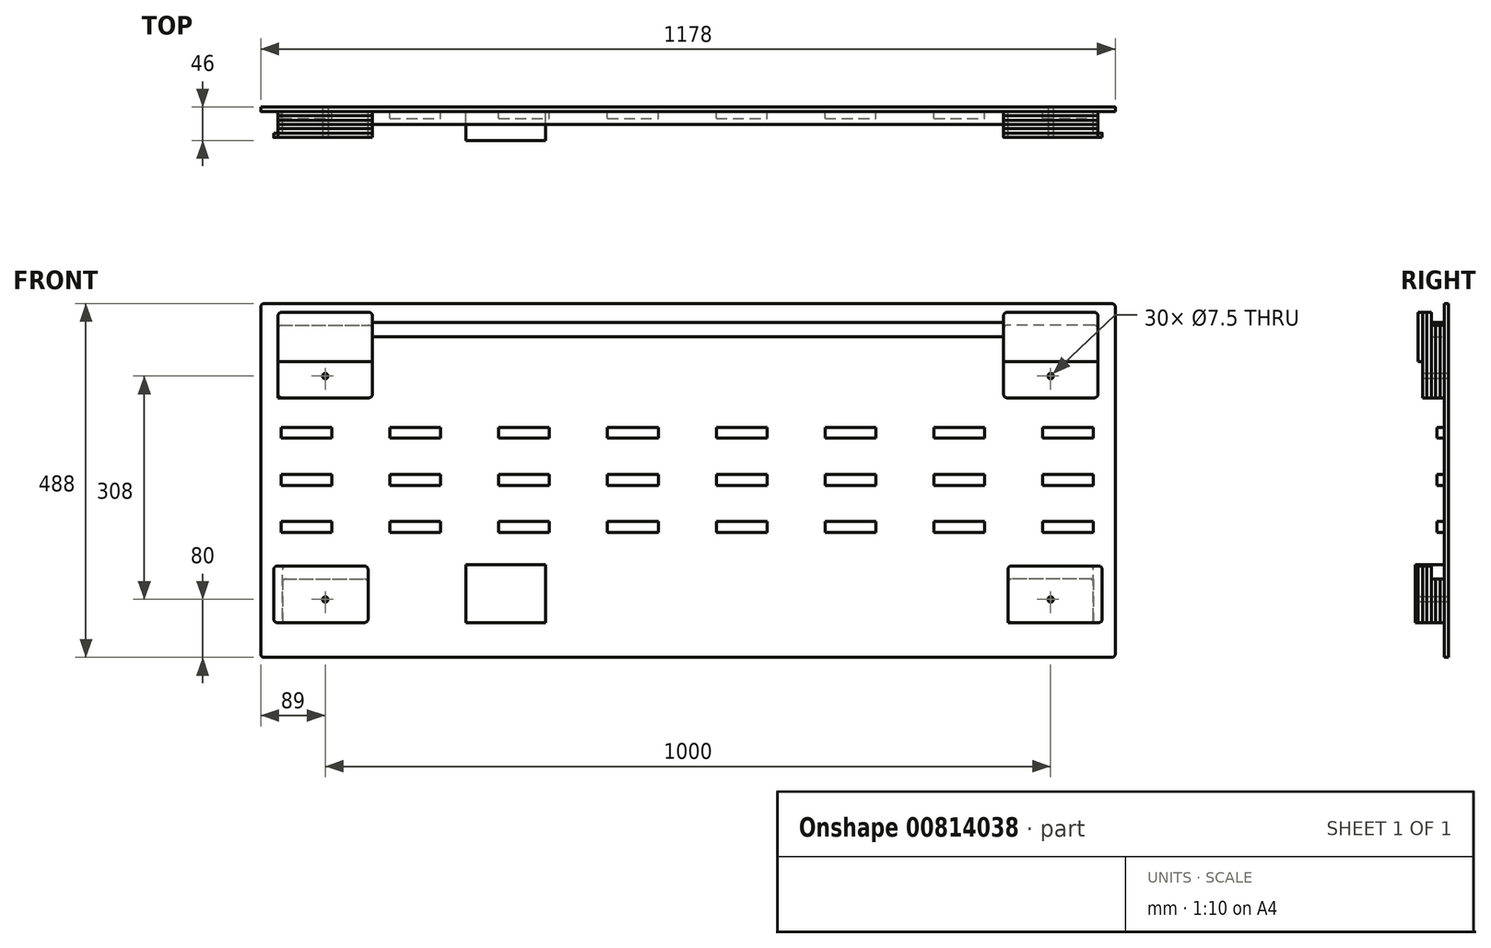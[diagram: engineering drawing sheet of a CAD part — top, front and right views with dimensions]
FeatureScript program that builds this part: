
annotation { "Feature Type Name" : "Feature", "Feature Type Description" : "" }
export const myFeature = defineFeature(function(context is Context, id is Id, definition is map)
    precondition{}
    {
        {
            var Q0;
            Q0=qCreatedBy(makeId("Front.planeOp"),FACE);
            var sketch = newSketch(context, id + "F0", { "sketchPlane" : qUnion([Q0])});
            skLineSegment(sketch, "E0.bottom", {"start": v(-589, 244) * mm, "end": v(589, 244) * mm});
            skLineSegment(sketch, "E0.top", {"start": v(-589, -244) * mm, "end": v(589, -244) * mm});
            skLineSegment(sketch, "E0.left", {"start": v(-589, 244) * mm, "end": v(-589, -244) * mm});
            skLineSegment(sketch, "E0.right", {"start": v(589, 244) * mm, "end": v(589, -244) * mm});
            skPoint(sketch, "E0.middle", {"position": v(0, 0) * mm});
            skSolve(sketch);
        }
        {
            var Q0;
            Q0 = qSketchRegion(id + "F0", true);
            extrude(context, id + "F1", {"entities" : qUnion([Q0]), "depth" : 6 * mm, "offsetDistance" : 25 * mm});
        }
        {
            var Q0;
            Q0=makeQuery(id+"F1.opExtrude","CAP_FACE",FACE,{"disambiguationData":[OSD([sQuery(id+"F0.wireOp",EDGE,"E0.bottom"),sQuery(id+"F0.wireOp",EDGE,"E0.top"),sQuery(id+"F0.wireOp",EDGE,"E0.left"),sQuery(id+"F0.wireOp",EDGE,"E0.right")])],"isStart":false});
            var sketch = newSketch(context, id + "F2", { "sketchPlane" : qUnion([Q0])});
            skLineSegment(sketch, "E1.bottom", {"start": v(-561, 73.35) * mm, "end": v(-491, 73.35) * mm});
            skLineSegment(sketch, "E1.top", {"start": v(-561, 58.35) * mm, "end": v(-491, 58.35) * mm});
            skLineSegment(sketch, "E1.left", {"start": v(-561, 73.35) * mm, "end": v(-561, 58.35) * mm});
            skLineSegment(sketch, "E1.right", {"start": v(-491, 73.35) * mm, "end": v(-491, 58.35) * mm});
            skLineSegment(sketch, "E2", {"start": v(-595.7, 2.32) * mm, "end": v(592.3, 2.32) * mm, "construction": true});
            skLineSegment(sketch, "E3", {"start": v(4.3, 246.32) * mm, "end": v(4.3, -241.68) * mm, "construction": true});
            skLineSegment(sketch, "E4", {"start": v(-595.7, 87.58) * mm, "end": v(592.3, 87.58) * mm, "construction": true});
            skLineSegment(sketch, "E5", {"start": v(-595.7, -82.94) * mm, "end": v(592.3, -82.94) * mm, "construction": true});
            skLineSegment(sketch, "E6", {"start": v(-565.56, 246.32) * mm, "end": v(-565.56, -241.68) * mm, "construction": true});
            skLineSegment(sketch, "E7", {"start": v(574.16, 246.32) * mm, "end": v(574.16, -241.68) * mm, "construction": true});
            skLineSegment(sketch, "E8.0.1.0", {"start": v(-561, 8.35) * mm, "end": v(-491, 8.35) * mm});
            skLineSegment(sketch, "E8.0.1.1", {"start": v(-491, 8.35) * mm, "end": v(-491, -6.65) * mm});
            skLineSegment(sketch, "E8.0.1.2", {"start": v(-561, 8.35) * mm, "end": v(-561, -6.65) * mm});
            skLineSegment(sketch, "E8.0.1.3", {"start": v(-561, -6.65) * mm, "end": v(-491, -6.65) * mm});
            skLineSegment(sketch, "E8.0.2.0", {"start": v(-561, -56.65) * mm, "end": v(-491, -56.65) * mm});
            skLineSegment(sketch, "E8.0.2.1", {"start": v(-491, -56.65) * mm, "end": v(-491, -71.65) * mm});
            skLineSegment(sketch, "E8.0.2.2", {"start": v(-561, -56.65) * mm, "end": v(-561, -71.65) * mm});
            skLineSegment(sketch, "E8.0.2.3", {"start": v(-561, -71.65) * mm, "end": v(-491, -71.65) * mm});
            skLineSegment(sketch, "E8.1.0.0", {"start": v(-411, 73.35) * mm, "end": v(-341, 73.35) * mm});
            skLineSegment(sketch, "E8.1.0.1", {"start": v(-341, 73.35) * mm, "end": v(-341, 58.35) * mm});
            skLineSegment(sketch, "E8.1.0.2", {"start": v(-411, 73.35) * mm, "end": v(-411, 58.35) * mm});
            skLineSegment(sketch, "E8.1.0.3", {"start": v(-411, 58.35) * mm, "end": v(-341, 58.35) * mm});
            skLineSegment(sketch, "E8.1.1.0", {"start": v(-411, 8.35) * mm, "end": v(-341, 8.35) * mm});
            skLineSegment(sketch, "E8.1.1.1", {"start": v(-341, 8.35) * mm, "end": v(-341, -6.65) * mm});
            skLineSegment(sketch, "E8.1.1.2", {"start": v(-411, 8.35) * mm, "end": v(-411, -6.65) * mm});
            skLineSegment(sketch, "E8.1.1.3", {"start": v(-411, -6.65) * mm, "end": v(-341, -6.65) * mm});
            skLineSegment(sketch, "E8.1.2.0", {"start": v(-411, -56.65) * mm, "end": v(-341, -56.65) * mm});
            skLineSegment(sketch, "E8.1.2.1", {"start": v(-341, -56.65) * mm, "end": v(-341, -71.65) * mm});
            skLineSegment(sketch, "E8.1.2.2", {"start": v(-411, -56.65) * mm, "end": v(-411, -71.65) * mm});
            skLineSegment(sketch, "E8.1.2.3", {"start": v(-411, -71.65) * mm, "end": v(-341, -71.65) * mm});
            skLineSegment(sketch, "E8.2.0.0", {"start": v(-261, 73.35) * mm, "end": v(-191, 73.35) * mm});
            skLineSegment(sketch, "E8.2.0.1", {"start": v(-191, 73.35) * mm, "end": v(-191, 58.35) * mm});
            skLineSegment(sketch, "E8.2.0.2", {"start": v(-261, 73.35) * mm, "end": v(-261, 58.35) * mm});
            skLineSegment(sketch, "E8.2.0.3", {"start": v(-261, 58.35) * mm, "end": v(-191, 58.35) * mm});
            skLineSegment(sketch, "E8.2.1.0", {"start": v(-261, 8.35) * mm, "end": v(-191, 8.35) * mm});
            skLineSegment(sketch, "E8.2.1.1", {"start": v(-191, 8.35) * mm, "end": v(-191, -6.65) * mm});
            skLineSegment(sketch, "E8.2.1.2", {"start": v(-261, 8.35) * mm, "end": v(-261, -6.65) * mm});
            skLineSegment(sketch, "E8.2.1.3", {"start": v(-261, -6.65) * mm, "end": v(-191, -6.65) * mm});
            skLineSegment(sketch, "E8.2.2.0", {"start": v(-261, -56.65) * mm, "end": v(-191, -56.65) * mm});
            skLineSegment(sketch, "E8.2.2.1", {"start": v(-191, -56.65) * mm, "end": v(-191, -71.65) * mm});
            skLineSegment(sketch, "E8.2.2.2", {"start": v(-261, -56.65) * mm, "end": v(-261, -71.65) * mm});
            skLineSegment(sketch, "E8.2.2.3", {"start": v(-261, -71.65) * mm, "end": v(-191, -71.65) * mm});
            skLineSegment(sketch, "E8.3.0.0", {"start": v(-111, 73.35) * mm, "end": v(-41, 73.35) * mm});
            skLineSegment(sketch, "E8.3.0.1", {"start": v(-41, 73.35) * mm, "end": v(-41, 58.35) * mm});
            skLineSegment(sketch, "E8.3.0.2", {"start": v(-111, 73.35) * mm, "end": v(-111, 58.35) * mm});
            skLineSegment(sketch, "E8.3.0.3", {"start": v(-111, 58.35) * mm, "end": v(-41, 58.35) * mm});
            skLineSegment(sketch, "E8.3.1.0", {"start": v(-111, 8.35) * mm, "end": v(-41, 8.35) * mm});
            skLineSegment(sketch, "E8.3.1.1", {"start": v(-41, 8.35) * mm, "end": v(-41, -6.65) * mm});
            skLineSegment(sketch, "E8.3.1.2", {"start": v(-111, 8.35) * mm, "end": v(-111, -6.65) * mm});
            skLineSegment(sketch, "E8.3.1.3", {"start": v(-111, -6.65) * mm, "end": v(-41, -6.65) * mm});
            skLineSegment(sketch, "E8.3.2.0", {"start": v(-111, -56.65) * mm, "end": v(-41, -56.65) * mm});
            skLineSegment(sketch, "E8.3.2.1", {"start": v(-41, -56.65) * mm, "end": v(-41, -71.65) * mm});
            skLineSegment(sketch, "E8.3.2.2", {"start": v(-111, -56.65) * mm, "end": v(-111, -71.65) * mm});
            skLineSegment(sketch, "E8.3.2.3", {"start": v(-111, -71.65) * mm, "end": v(-41, -71.65) * mm});
            skLineSegment(sketch, "E8.4.0.0", {"start": v(39, 73.35) * mm, "end": v(109, 73.35) * mm});
            skLineSegment(sketch, "E8.4.0.1", {"start": v(109, 73.35) * mm, "end": v(109, 58.35) * mm});
            skLineSegment(sketch, "E8.4.0.2", {"start": v(39, 73.35) * mm, "end": v(39, 58.35) * mm});
            skLineSegment(sketch, "E8.4.0.3", {"start": v(39, 58.35) * mm, "end": v(109, 58.35) * mm});
            skLineSegment(sketch, "E8.4.1.0", {"start": v(39, 8.35) * mm, "end": v(109, 8.35) * mm});
            skLineSegment(sketch, "E8.4.1.1", {"start": v(109, 8.35) * mm, "end": v(109, -6.65) * mm});
            skLineSegment(sketch, "E8.4.1.2", {"start": v(39, 8.35) * mm, "end": v(39, -6.65) * mm});
            skLineSegment(sketch, "E8.4.1.3", {"start": v(39, -6.65) * mm, "end": v(109, -6.65) * mm});
            skLineSegment(sketch, "E8.4.2.0", {"start": v(39, -56.65) * mm, "end": v(109, -56.65) * mm});
            skLineSegment(sketch, "E8.4.2.1", {"start": v(109, -56.65) * mm, "end": v(109, -71.65) * mm});
            skLineSegment(sketch, "E8.4.2.2", {"start": v(39, -56.65) * mm, "end": v(39, -71.65) * mm});
            skLineSegment(sketch, "E8.4.2.3", {"start": v(39, -71.65) * mm, "end": v(109, -71.65) * mm});
            skLineSegment(sketch, "E8.5.0.0", {"start": v(189, 73.35) * mm, "end": v(259, 73.35) * mm});
            skLineSegment(sketch, "E8.5.0.1", {"start": v(259, 73.35) * mm, "end": v(259, 58.35) * mm});
            skLineSegment(sketch, "E8.5.0.2", {"start": v(189, 73.35) * mm, "end": v(189, 58.35) * mm});
            skLineSegment(sketch, "E8.5.0.3", {"start": v(189, 58.35) * mm, "end": v(259, 58.35) * mm});
            skLineSegment(sketch, "E8.5.1.0", {"start": v(189, 8.35) * mm, "end": v(259, 8.35) * mm});
            skLineSegment(sketch, "E8.5.1.1", {"start": v(259, 8.35) * mm, "end": v(259, -6.65) * mm});
            skLineSegment(sketch, "E8.5.1.2", {"start": v(189, 8.35) * mm, "end": v(189, -6.65) * mm});
            skLineSegment(sketch, "E8.5.1.3", {"start": v(189, -6.65) * mm, "end": v(259, -6.65) * mm});
            skLineSegment(sketch, "E8.5.2.0", {"start": v(189, -56.65) * mm, "end": v(259, -56.65) * mm});
            skLineSegment(sketch, "E8.5.2.1", {"start": v(259, -56.65) * mm, "end": v(259, -71.65) * mm});
            skLineSegment(sketch, "E8.5.2.2", {"start": v(189, -56.65) * mm, "end": v(189, -71.65) * mm});
            skLineSegment(sketch, "E8.5.2.3", {"start": v(189, -71.65) * mm, "end": v(259, -71.65) * mm});
            skLineSegment(sketch, "E8.6.0.0", {"start": v(339, 73.35) * mm, "end": v(409, 73.35) * mm});
            skLineSegment(sketch, "E8.6.0.1", {"start": v(409, 73.35) * mm, "end": v(409, 58.35) * mm});
            skLineSegment(sketch, "E8.6.0.2", {"start": v(339, 73.35) * mm, "end": v(339, 58.35) * mm});
            skLineSegment(sketch, "E8.6.0.3", {"start": v(339, 58.35) * mm, "end": v(409, 58.35) * mm});
            skLineSegment(sketch, "E8.6.1.0", {"start": v(339, 8.35) * mm, "end": v(409, 8.35) * mm});
            skLineSegment(sketch, "E8.6.1.1", {"start": v(409, 8.35) * mm, "end": v(409, -6.65) * mm});
            skLineSegment(sketch, "E8.6.1.2", {"start": v(339, 8.35) * mm, "end": v(339, -6.65) * mm});
            skLineSegment(sketch, "E8.6.1.3", {"start": v(339, -6.65) * mm, "end": v(409, -6.65) * mm});
            skLineSegment(sketch, "E8.6.2.0", {"start": v(339, -56.65) * mm, "end": v(409, -56.65) * mm});
            skLineSegment(sketch, "E8.6.2.1", {"start": v(409, -56.65) * mm, "end": v(409, -71.65) * mm});
            skLineSegment(sketch, "E8.6.2.2", {"start": v(339, -56.65) * mm, "end": v(339, -71.65) * mm});
            skLineSegment(sketch, "E8.6.2.3", {"start": v(339, -71.65) * mm, "end": v(409, -71.65) * mm});
            skLineSegment(sketch, "E8.7.0.0", {"start": v(489, 73.35) * mm, "end": v(559, 73.35) * mm});
            skLineSegment(sketch, "E8.7.0.1", {"start": v(559, 73.35) * mm, "end": v(559, 58.35) * mm});
            skLineSegment(sketch, "E8.7.0.2", {"start": v(489, 73.35) * mm, "end": v(489, 58.35) * mm});
            skLineSegment(sketch, "E8.7.0.3", {"start": v(489, 58.35) * mm, "end": v(559, 58.35) * mm});
            skLineSegment(sketch, "E8.7.1.0", {"start": v(489, 8.35) * mm, "end": v(559, 8.35) * mm});
            skLineSegment(sketch, "E8.7.1.1", {"start": v(559, 8.35) * mm, "end": v(559, -6.65) * mm});
            skLineSegment(sketch, "E8.7.1.2", {"start": v(489, 8.35) * mm, "end": v(489, -6.65) * mm});
            skLineSegment(sketch, "E8.7.1.3", {"start": v(489, -6.65) * mm, "end": v(559, -6.65) * mm});
            skLineSegment(sketch, "E8.7.2.0", {"start": v(489, -56.65) * mm, "end": v(559, -56.65) * mm});
            skLineSegment(sketch, "E8.7.2.1", {"start": v(559, -56.65) * mm, "end": v(559, -71.65) * mm});
            skLineSegment(sketch, "E8.7.2.2", {"start": v(489, -56.65) * mm, "end": v(489, -71.65) * mm});
            skLineSegment(sketch, "E8.7.2.3", {"start": v(489, -71.65) * mm, "end": v(559, -71.65) * mm});
            skLineSegment(sketch, "E8.direction1", {"start": v(-561, 58.35) * mm, "end": v(-411, 58.35) * mm, "construction": true});
            skLineSegment(sketch, "E8.direction2", {"start": v(-561, 58.35) * mm, "end": v(-561, -6.65) * mm, "construction": true});
            skSolve(sketch);
        }
        {
            var Q0;
            Q0 = qSketchRegion(id + "F2", true);
            extrude(context, id + "F3", {"entities" : qUnion([Q0]), "depth" : 10 * mm, "offsetDistance" : 25 * mm});
        }
        {
            var Q0;
            Q0=makeQuery(id+"F1.opExtrude","CAP_FACE",FACE,{"disambiguationData":[OSD([sQuery(id+"F0.wireOp",EDGE,"E0.bottom"),sQuery(id+"F0.wireOp",EDGE,"E0.top"),sQuery(id+"F0.wireOp",EDGE,"E0.left"),sQuery(id+"F0.wireOp",EDGE,"E0.right")])],"isStart":false});
            var sketch = newSketch(context, id + "F4", { "sketchPlane" : qUnion([Q0])});
            skLineSegment(sketch, "E9", {"start": v(-500, 275.35) * mm, "end": v(-500, -293.54) * mm, "construction": true});
            skLineSegment(sketch, "E10", {"start": v(500, 293.4) * mm, "end": v(500, -305.65) * mm, "construction": true});
            skLineSegment(sketch, "E11.bottom", {"start": v(-565, 214) * mm, "end": v(-435, 214) * mm});
            skLineSegment(sketch, "E11.top", {"start": v(-565, 114) * mm, "end": v(-435, 114) * mm});
            skLineSegment(sketch, "E11.left", {"start": v(-565, 214) * mm, "end": v(-565, 114) * mm});
            skLineSegment(sketch, "E11.right", {"start": v(-435, 214) * mm, "end": v(-435, 114) * mm});
            skPoint(sketch, "E11.middle", {"position": v(-500, 164) * mm});
            skLineSegment(sketch, "E12.MirrorCS", {"start": v(565, 114) * mm, "end": v(435, 114) * mm});
            skPoint(sketch, "E13.MirrorP", {"position": v(500, 164) * mm});
            skLineSegment(sketch, "E14.MirrorCS", {"start": v(565, 214) * mm, "end": v(435, 214) * mm});
            skLineSegment(sketch, "E15.MirrorCS", {"start": v(565, 214) * mm, "end": v(565, 114) * mm});
            skLineSegment(sketch, "E16.MirrorCS", {"start": v(435, 214) * mm, "end": v(435, 114) * mm});
            skLineSegment(sketch, "E17", {"start": v(-559, 288) * mm, "end": v(-559, -276.63) * mm, "construction": true});
            skLineSegment(sketch, "E18", {"start": v(559, 296.65) * mm, "end": v(559, -367.71) * mm, "construction": true});
            skLineSegment(sketch, "E19.bottom", {"start": v(-559, -136) * mm, "end": v(-441, -136) * mm});
            skLineSegment(sketch, "E19.top", {"start": v(-559, -196) * mm, "end": v(-441, -196) * mm});
            skLineSegment(sketch, "E19.left", {"start": v(-559, -136) * mm, "end": v(-559, -196) * mm});
            skLineSegment(sketch, "E19.right", {"start": v(-441, -136) * mm, "end": v(-441, -196) * mm});
            skPoint(sketch, "E19.middle", {"position": v(-500, -166) * mm});
            skLineSegment(sketch, "E20.MirrorCS", {"start": v(559, -136) * mm, "end": v(441, -136) * mm});
            skLineSegment(sketch, "E21.MirrorCS", {"start": v(441, -136) * mm, "end": v(441, -196) * mm});
            skLineSegment(sketch, "E22.MirrorCS", {"start": v(559, -136) * mm, "end": v(559, -196) * mm});
            skLineSegment(sketch, "E23.MirrorCS", {"start": v(559, -196) * mm, "end": v(441, -196) * mm});
            skPoint(sketch, "E24.MirrorP", {"position": v(500, -166) * mm});
            skSolve(sketch);
        }
        {
            var Q0;
            Q0 = qSketchRegion(id + "F4", true);
            extrude(context, id + "F5", {"entities" : qUnion([Q0]), "depth" : 6 * mm, "offsetDistance" : 25 * mm});
        }
        {
            var Q0;
            Q0 = qSketchRegion(id + "F4", true);
            extrude(context, id + "F6", {"entities" : qUnion([Q0]), "depth" : 6 * mm, "offsetDistance" : 25 * mm});
        }
        {
            var Q0;
            Q0=makeQuery(id+"F5.opExtrude","SWEPT_EDGE",EDGE,{"disambiguationData":[OSD([sQuery(id+"F4.wireOp",EDGE,"E11.bottom"),sQuery(id+"F4.wireOp",EDGE,"E11.left")])]});
            var Q1;
            Q1=makeQuery(id+"F5.opExtrude","SWEPT_EDGE",EDGE,{"disambiguationData":[OSD([sQuery(id+"F4.wireOp",EDGE,"E11.top"),sQuery(id+"F4.wireOp",EDGE,"E11.left")])]});
            var Q2;
            Q2=makeQuery(id+"F5.opExtrude","SWEPT_EDGE",EDGE,{"disambiguationData":[OSD([sQuery(id+"F4.wireOp",EDGE,"E11.bottom"),sQuery(id+"F4.wireOp",EDGE,"E11.right")])]});
            var Q3;
            Q3=makeQuery(id+"F5.opExtrude","SWEPT_EDGE",EDGE,{"disambiguationData":[OSD([sQuery(id+"F4.wireOp",EDGE,"E11.top"),sQuery(id+"F4.wireOp",EDGE,"E11.right")])]});
            var Q4;
            Q4=makeQuery(id+"F5.opExtrude","SWEPT_EDGE",EDGE,{"disambiguationData":[OSD([sQuery(id+"F4.wireOp",EDGE,"c781e211-af4b-461f-87b0-653b7e23daed2.MirrorCS"),sQuery(id+"F4.wireOp",EDGE,"c781e211-af4b-461f-87b0-653b7e23daed7.MirrorCS")])]});
            var Q5;
            Q5=makeQuery(id+"F5.opExtrude","SWEPT_EDGE",EDGE,{"disambiguationData":[OSD([sQuery(id+"F4.wireOp",EDGE,"c781e211-af4b-461f-87b0-653b7e23daed2.MirrorCS"),sQuery(id+"F4.wireOp",EDGE,"c781e211-af4b-461f-87b0-653b7e23daed4.MirrorCS")])]});
            var Q6;
            Q6=makeQuery(id+"F5.opExtrude","SWEPT_EDGE",EDGE,{"disambiguationData":[OSD([sQuery(id+"F4.wireOp",EDGE,"c781e211-af4b-461f-87b0-653b7e23daed0.MirrorCS"),sQuery(id+"F4.wireOp",EDGE,"c781e211-af4b-461f-87b0-653b7e23daed7.MirrorCS")])]});
            var Q7;
            Q7=makeQuery(id+"F5.opExtrude","SWEPT_EDGE",EDGE,{"disambiguationData":[OSD([sQuery(id+"F4.wireOp",EDGE,"c781e211-af4b-461f-87b0-653b7e23daed0.MirrorCS"),sQuery(id+"F4.wireOp",EDGE,"c781e211-af4b-461f-87b0-653b7e23daed4.MirrorCS")])]});
            var Q8;
            Q8=makeQuery(id+"F5.opExtrude","SWEPT_EDGE",EDGE,{"disambiguationData":[OSD([sQuery(id+"F4.wireOp",EDGE,"c781e211-af4b-461f-87b0-653b7e23daed3.MirrorCS"),sQuery(id+"F4.wireOp",EDGE,"c781e211-af4b-461f-87b0-653b7e23daed5.MirrorCS")])]});
            var Q9;
            Q9=makeQuery(id+"F5.opExtrude","SWEPT_EDGE",EDGE,{"disambiguationData":[OSD([sQuery(id+"F4.wireOp",EDGE,"c781e211-af4b-461f-87b0-653b7e23daed1.MirrorCS"),sQuery(id+"F4.wireOp",EDGE,"c781e211-af4b-461f-87b0-653b7e23daed5.MirrorCS")])]});
            var Q10;
            Q10=makeQuery(id+"F5.opExtrude","SWEPT_EDGE",EDGE,{"disambiguationData":[OSD([sQuery(id+"F4.wireOp",EDGE,"c781e211-af4b-461f-87b0-653b7e23daed1.MirrorCS"),sQuery(id+"F4.wireOp",EDGE,"c781e211-af4b-461f-87b0-653b7e23daed6.MirrorCS")])]});
            var Q11;
            Q11=makeQuery(id+"F5.opExtrude","SWEPT_EDGE",EDGE,{"disambiguationData":[OSD([sQuery(id+"F4.wireOp",EDGE,"c781e211-af4b-461f-87b0-653b7e23daed3.MirrorCS"),sQuery(id+"F4.wireOp",EDGE,"c781e211-af4b-461f-87b0-653b7e23daed6.MirrorCS")])]});
            var Q12;
            Q12=makeQuery(id+"F5.opExtrude","SWEPT_EDGE",EDGE,{"disambiguationData":[OSD([sQuery(id+"F4.wireOp",EDGE,"E12.MirrorCS"),sQuery(id+"F4.wireOp",EDGE,"E16.MirrorCS")])]});
            var Q13;
            Q13=makeQuery(id+"F5.opExtrude","SWEPT_EDGE",EDGE,{"disambiguationData":[OSD([sQuery(id+"F4.wireOp",EDGE,"E12.MirrorCS"),sQuery(id+"F4.wireOp",EDGE,"E15.MirrorCS")])]});
            var Q14;
            Q14=makeQuery(id+"F5.opExtrude","SWEPT_EDGE",EDGE,{"disambiguationData":[OSD([sQuery(id+"F4.wireOp",EDGE,"E14.MirrorCS"),sQuery(id+"F4.wireOp",EDGE,"E16.MirrorCS")])]});
            var Q15;
            Q15=makeQuery(id+"F5.opExtrude","SWEPT_EDGE",EDGE,{"disambiguationData":[OSD([sQuery(id+"F4.wireOp",EDGE,"E14.MirrorCS"),sQuery(id+"F4.wireOp",EDGE,"E15.MirrorCS")])]});
            fillet(context, id + "F7", {"entities" : qUnion([Q0, Q1, Q2, Q3, Q4, Q5, Q6, Q7, Q8, Q9, Q10, Q11, Q12, Q13, Q14, Q15]), "radius" : 5 * mm, "tangentPropagation" : true, "allowEdgeOverflow" : false});
        }
        {
            var Q0;
            Q0=makeQuery(id+"F5.opExtrude","CAP_FACE",FACE,{"disambiguationData":[OSD([sQuery(id+"F4.wireOp",EDGE,"E11.bottom"),sQuery(id+"F4.wireOp",EDGE,"E11.top"),sQuery(id+"F4.wireOp",EDGE,"E11.left"),sQuery(id+"F4.wireOp",EDGE,"E11.right")])],"isStart":false});
            var sketch = newSketch(context, id + "F8", { "sketchPlane" : qUnion([Q0])});
            skLineSegment(sketch, "E25.bottom", {"start": v(-565, 214) * mm, "end": v(-435, 214) * mm});
            skLineSegment(sketch, "E25.top", {"start": v(-565, 114) * mm, "end": v(-435, 114) * mm});
            skLineSegment(sketch, "E25.left", {"start": v(-565, 214) * mm, "end": v(-565, 114) * mm});
            skLineSegment(sketch, "E25.right", {"start": v(-435, 214) * mm, "end": v(-435, 114) * mm});
            skPoint(sketch, "E25.middle", {"position": v(-500, 164) * mm});
            skPoint(sketch, "E25.middle.positionSnap0", {"position": v(-565, 164) * mm});
            skPoint(sketch, "E25.middle.positionSnap1", {"position": v(-500, 114) * mm});
            skPoint(sketch, "E25.centerSnap0", {"position": v(-565, 164) * mm});
            skPoint(sketch, "E25.centerSnap1", {"position": v(-500, 114) * mm});
            skPoint(sketch, "E26.MirrorP", {"position": v(500, 114) * mm});
            skPoint(sketch, "E27.MirrorP", {"position": v(565, 164) * mm});
            skLineSegment(sketch, "E28.MirrorCS", {"start": v(435, 214) * mm, "end": v(435, 114) * mm});
            skPoint(sketch, "E29.MirrorP", {"position": v(500, 164) * mm});
            skLineSegment(sketch, "E30.MirrorCS", {"start": v(565, 214) * mm, "end": v(565, 114) * mm});
            skLineSegment(sketch, "E31.MirrorCS", {"start": v(565, 114) * mm, "end": v(435, 114) * mm});
            skLineSegment(sketch, "E32.MirrorCS", {"start": v(565, 214) * mm, "end": v(435, 214) * mm});
            skLineSegment(sketch, "E33.bottom", {"start": v(-559, -196) * mm, "end": v(-441, -196) * mm});
            skLineSegment(sketch, "E33.top", {"start": v(-559, -136) * mm, "end": v(-441, -136) * mm});
            skLineSegment(sketch, "E33.left", {"start": v(-559, -196) * mm, "end": v(-559, -136) * mm});
            skLineSegment(sketch, "E33.right", {"start": v(-441, -196) * mm, "end": v(-441, -136) * mm});
            skLineSegment(sketch, "E34.MirrorCS", {"start": v(559, -196) * mm, "end": v(441, -196) * mm});
            skLineSegment(sketch, "E35.MirrorCS", {"start": v(559, -196) * mm, "end": v(559, -136) * mm});
            skLineSegment(sketch, "E36.MirrorCS", {"start": v(559, -136) * mm, "end": v(441, -136) * mm});
            skLineSegment(sketch, "E37.MirrorCS", {"start": v(441, -196) * mm, "end": v(441, -136) * mm});
            skSolve(sketch);
        }
        {
            var Q0;
            Q0 = qSketchRegion(id + "F8", true);
            extrude(context, id + "F9", {"entities" : qUnion([Q0]), "depth" : 6 * mm, "offsetDistance" : 25 * mm});
        }
        {
            var Q0;
            Q0=makeQuery(id+"F9.opExtrude","CAP_FACE",FACE,{"disambiguationData":[OSD([sQuery(id+"F8.wireOp",EDGE,"E25.bottom"),sQuery(id+"F8.wireOp",EDGE,"E25.top"),sQuery(id+"F8.wireOp",EDGE,"E25.left"),sQuery(id+"F8.wireOp",EDGE,"E25.right")])],"isStart":false});
            var sketch = newSketch(context, id + "F10", { "sketchPlane" : qUnion([Q0])});
            skLineSegment(sketch, "E38.bottom", {"start": v(-565, 214) * mm, "end": v(-435, 214) * mm});
            skLineSegment(sketch, "E38.top", {"start": v(-565, 114) * mm, "end": v(-435, 114) * mm});
            skLineSegment(sketch, "E38.left", {"start": v(-565, 214) * mm, "end": v(-565, 114) * mm});
            skLineSegment(sketch, "E38.right", {"start": v(-435, 214) * mm, "end": v(-435, 114) * mm});
            skPoint(sketch, "E38.middle", {"position": v(-500, 164) * mm});
            skPoint(sketch, "E38.middle.positionSnap0", {"position": v(-565, 164) * mm});
            skPoint(sketch, "E38.middle.positionSnap1", {"position": v(-500, 114) * mm});
            skPoint(sketch, "E38.centerSnap0", {"position": v(-565, 164) * mm});
            skPoint(sketch, "E38.centerSnap1", {"position": v(-500, 114) * mm});
            skPoint(sketch, "E39.MirrorP", {"position": v(565, 164) * mm});
            skPoint(sketch, "E40.MirrorP", {"position": v(500, 114) * mm});
            skLineSegment(sketch, "E41.MirrorCS", {"start": v(565, 114) * mm, "end": v(435, 114) * mm});
            skLineSegment(sketch, "E42.MirrorCS", {"start": v(565, 214) * mm, "end": v(435, 214) * mm});
            skPoint(sketch, "E43.MirrorP", {"position": v(500, 164) * mm});
            skLineSegment(sketch, "E44.MirrorCS", {"start": v(435, 214) * mm, "end": v(435, 114) * mm});
            skLineSegment(sketch, "E45.MirrorCS", {"start": v(565, 214) * mm, "end": v(565, 114) * mm});
            skLineSegment(sketch, "E46.bottom", {"start": v(-559, -196) * mm, "end": v(-441, -196) * mm});
            skLineSegment(sketch, "E46.top", {"start": v(-559, -136) * mm, "end": v(-441, -136) * mm});
            skLineSegment(sketch, "E46.left", {"start": v(-559, -196) * mm, "end": v(-559, -136) * mm});
            skLineSegment(sketch, "E46.right", {"start": v(-441, -196) * mm, "end": v(-441, -136) * mm});
            skLineSegment(sketch, "E47.MirrorCS", {"start": v(559, -196) * mm, "end": v(559, -136) * mm});
            skLineSegment(sketch, "E48.MirrorCS", {"start": v(559, -136) * mm, "end": v(441, -136) * mm});
            skLineSegment(sketch, "E49.MirrorCS", {"start": v(559, -196) * mm, "end": v(441, -196) * mm});
            skLineSegment(sketch, "E50.MirrorCS", {"start": v(441, -196) * mm, "end": v(441, -136) * mm});
            skSolve(sketch);
        }
        {
            var Q0;
            Q0 = qSketchRegion(id + "F10", true);
            extrude(context, id + "F11", {"entities" : qUnion([Q0]), "depth" : 6 * mm, "offsetDistance" : 25 * mm});
        }
        {
            var Q0;
            Q0=makeQuery(id+"F11.opExtrude","CAP_FACE",FACE,{"disambiguationData":[OSD([sQuery(id+"F10.wireOp",EDGE,"E38.bottom"),sQuery(id+"F10.wireOp",EDGE,"E38.top"),sQuery(id+"F10.wireOp",EDGE,"E38.left"),sQuery(id+"F10.wireOp",EDGE,"E38.right")])],"isStart":false});
            var sketch = newSketch(context, id + "F12", { "sketchPlane" : qUnion([Q0])});
            skLineSegment(sketch, "E51.bottom", {"start": v(-565, 114) * mm, "end": v(-435, 114) * mm});
            skLineSegment(sketch, "E51.top", {"start": v(-565, 232) * mm, "end": v(-435, 232) * mm});
            skLineSegment(sketch, "E51.left", {"start": v(-565, 114) * mm, "end": v(-565, 232) * mm});
            skLineSegment(sketch, "E51.right", {"start": v(-435, 114) * mm, "end": v(-435, 232) * mm});
            skLineSegment(sketch, "E52.MirrorCS", {"start": v(565, 114) * mm, "end": v(565, 232) * mm});
            skLineSegment(sketch, "E53.MirrorCS", {"start": v(565, 114) * mm, "end": v(435, 114) * mm});
            skLineSegment(sketch, "E54.MirrorCS", {"start": v(565, 232) * mm, "end": v(435, 232) * mm});
            skLineSegment(sketch, "E55.MirrorCS", {"start": v(435, 114) * mm, "end": v(435, 232) * mm});
            skLineSegment(sketch, "E56.bottom", {"start": v(-559, -196) * mm, "end": v(-441, -196) * mm});
            skLineSegment(sketch, "E56.top", {"start": v(-559, -118) * mm, "end": v(-441, -118) * mm});
            skLineSegment(sketch, "E56.left", {"start": v(-559, -196) * mm, "end": v(-559, -118) * mm});
            skLineSegment(sketch, "E56.right", {"start": v(-441, -196) * mm, "end": v(-441, -118) * mm});
            skLineSegment(sketch, "E57.MirrorCS", {"start": v(559, -118) * mm, "end": v(441, -118) * mm});
            skLineSegment(sketch, "E58.MirrorCS", {"start": v(559, -196) * mm, "end": v(441, -196) * mm});
            skLineSegment(sketch, "E59.MirrorCS", {"start": v(559, -196) * mm, "end": v(559, -118) * mm});
            skLineSegment(sketch, "E60.MirrorCS", {"start": v(441, -196) * mm, "end": v(441, -118) * mm});
            skSolve(sketch);
        }
        {
            var Q0;
            Q0 = qSketchRegion(id + "F12", true);
            extrude(context, id + "F13", {"entities" : qUnion([Q0]), "depth" : 6 * mm, "offsetDistance" : 25 * mm});
        }
        {
            var Q0;
            Q0=makeQuery(id+"F13.opExtrude","CAP_FACE",FACE,{"disambiguationData":[OSD([sQuery(id+"F12.wireOp",EDGE,"E51.bottom"),sQuery(id+"F12.wireOp",EDGE,"E51.top"),sQuery(id+"F12.wireOp",EDGE,"E51.left"),sQuery(id+"F12.wireOp",EDGE,"E51.right")])],"isStart":false});
            var sketch = newSketch(context, id + "F14", { "sketchPlane" : qUnion([Q0])});
            skLineSegment(sketch, "E61.bottom", {"start": v(-565, 232) * mm, "end": v(-435, 232) * mm});
            skLineSegment(sketch, "E61.top", {"start": v(-565, 114) * mm, "end": v(-435, 114) * mm});
            skLineSegment(sketch, "E61.left", {"start": v(-565, 232) * mm, "end": v(-565, 114) * mm});
            skLineSegment(sketch, "E61.right", {"start": v(-435, 232) * mm, "end": v(-435, 114) * mm});
            skLineSegment(sketch, "E62.MirrorCS", {"start": v(565, 232) * mm, "end": v(565, 114) * mm});
            skLineSegment(sketch, "E63.MirrorCS", {"start": v(435, 232) * mm, "end": v(435, 114) * mm});
            skLineSegment(sketch, "E64.MirrorCS", {"start": v(565, 232) * mm, "end": v(435, 232) * mm});
            skLineSegment(sketch, "E65.MirrorCS", {"start": v(565, 114) * mm, "end": v(435, 114) * mm});
            skLineSegment(sketch, "E66.bottom", {"start": v(-559, -118) * mm, "end": v(-441, -118) * mm});
            skLineSegment(sketch, "E66.top", {"start": v(-559, -196) * mm, "end": v(-441, -196) * mm});
            skLineSegment(sketch, "E66.left", {"start": v(-559, -118) * mm, "end": v(-559, -196) * mm});
            skLineSegment(sketch, "E66.right", {"start": v(-441, -118) * mm, "end": v(-441, -196) * mm});
            skLineSegment(sketch, "E67.MirrorCS", {"start": v(559, -118) * mm, "end": v(559, -196) * mm});
            skLineSegment(sketch, "E68.MirrorCS", {"start": v(559, -118) * mm, "end": v(441, -118) * mm});
            skLineSegment(sketch, "E69.MirrorCS", {"start": v(559, -196) * mm, "end": v(441, -196) * mm});
            skLineSegment(sketch, "E70.MirrorCS", {"start": v(441, -118) * mm, "end": v(441, -196) * mm});
            skSolve(sketch);
        }
        {
            var Q0;
            Q0 = qSketchRegion(id + "F14", true);
            extrude(context, id + "F15", {"entities" : qUnion([Q0]), "depth" : 6 * mm, "offsetDistance" : 25 * mm});
        }
        {
            var Q0;
            Q0=makeQuery(id+"F9.opExtrude","SWEPT_EDGE",EDGE,{"disambiguationData":[OSD([sQuery(id+"F8.wireOp",EDGE,"E25.bottom"),sQuery(id+"F8.wireOp",EDGE,"E25.left")])]});
            var Q1;
            Q1=makeQuery(id+"F11.opExtrude","SWEPT_EDGE",EDGE,{"disambiguationData":[OSD([sQuery(id+"F10.wireOp",EDGE,"E38.bottom"),sQuery(id+"F10.wireOp",EDGE,"E38.left")])]});
            var Q2;
            Q2=makeQuery(id+"F13.opExtrude","SWEPT_EDGE",EDGE,{"disambiguationData":[OSD([sQuery(id+"F12.wireOp",EDGE,"E51.top"),sQuery(id+"F12.wireOp",EDGE,"E51.left")])]});
            var Q3;
            Q3=makeQuery(id+"F15.opExtrude","SWEPT_EDGE",EDGE,{"disambiguationData":[OSD([sQuery(id+"F14.wireOp",EDGE,"E61.bottom"),sQuery(id+"F14.wireOp",EDGE,"E61.left")])]});
            var Q4;
            Q4=makeQuery(id+"F9.opExtrude","SWEPT_EDGE",EDGE,{"disambiguationData":[OSD([sQuery(id+"F8.wireOp",EDGE,"E25.top"),sQuery(id+"F8.wireOp",EDGE,"E25.left")])]});
            var Q5;
            Q5=makeQuery(id+"F11.opExtrude","SWEPT_EDGE",EDGE,{"disambiguationData":[OSD([sQuery(id+"F10.wireOp",EDGE,"E38.top"),sQuery(id+"F10.wireOp",EDGE,"E38.left")])]});
            var Q6;
            Q6=makeQuery(id+"F13.opExtrude","SWEPT_EDGE",EDGE,{"disambiguationData":[OSD([sQuery(id+"F12.wireOp",EDGE,"E51.bottom"),sQuery(id+"F12.wireOp",EDGE,"E51.left")])]});
            var Q7;
            Q7=makeQuery(id+"F15.opExtrude","SWEPT_EDGE",EDGE,{"disambiguationData":[OSD([sQuery(id+"F14.wireOp",EDGE,"E61.top"),sQuery(id+"F14.wireOp",EDGE,"E61.left")])]});
            var Q8;
            Q8=makeQuery(id+"F9.opExtrude","SWEPT_EDGE",EDGE,{"disambiguationData":[OSD([sQuery(id+"F8.wireOp",EDGE,"E25.top"),sQuery(id+"F8.wireOp",EDGE,"E25.right")])]});
            var Q9;
            Q9=makeQuery(id+"F9.opExtrude","SWEPT_EDGE",EDGE,{"disambiguationData":[OSD([sQuery(id+"F8.wireOp",EDGE,"E25.bottom"),sQuery(id+"F8.wireOp",EDGE,"E25.right")])]});
            var Q10;
            Q10=makeQuery(id+"F11.opExtrude","SWEPT_EDGE",EDGE,{"disambiguationData":[OSD([sQuery(id+"F10.wireOp",EDGE,"E38.top"),sQuery(id+"F10.wireOp",EDGE,"E38.right")])]});
            var Q11;
            Q11=makeQuery(id+"F11.opExtrude","SWEPT_EDGE",EDGE,{"disambiguationData":[OSD([sQuery(id+"F10.wireOp",EDGE,"E38.bottom"),sQuery(id+"F10.wireOp",EDGE,"E38.right")])]});
            var Q12;
            Q12=makeQuery(id+"F13.opExtrude","SWEPT_EDGE",EDGE,{"disambiguationData":[OSD([sQuery(id+"F12.wireOp",EDGE,"E51.bottom"),sQuery(id+"F12.wireOp",EDGE,"E51.right")])]});
            var Q13;
            Q13=makeQuery(id+"F13.opExtrude","SWEPT_EDGE",EDGE,{"disambiguationData":[OSD([sQuery(id+"F12.wireOp",EDGE,"E51.top"),sQuery(id+"F12.wireOp",EDGE,"E51.right")])]});
            var Q14;
            Q14=makeQuery(id+"F15.opExtrude","SWEPT_EDGE",EDGE,{"disambiguationData":[OSD([sQuery(id+"F14.wireOp",EDGE,"E61.top"),sQuery(id+"F14.wireOp",EDGE,"E61.right")])]});
            var Q15;
            Q15=makeQuery(id+"F15.opExtrude","SWEPT_EDGE",EDGE,{"disambiguationData":[OSD([sQuery(id+"F14.wireOp",EDGE,"E61.bottom"),sQuery(id+"F14.wireOp",EDGE,"E61.right")])]});
            var Q16;
            Q16=makeQuery(id+"F6.opExtrude","SWEPT_EDGE",EDGE,{"disambiguationData":[OSD([sQuery(id+"F4.wireOp",EDGE,"E11.top"),sQuery(id+"F4.wireOp",EDGE,"E11.right")])]});
            var Q17;
            Q17=makeQuery(id+"F5.opExtrude","SWEPT_EDGE",EDGE,{"disambiguationData":[OSD([sQuery(id+"F4.wireOp",EDGE,"E19.bottom"),sQuery(id+"F4.wireOp",EDGE,"E19.left")])]});
            var Q18;
            Q18=makeQuery(id+"F9.opExtrude","SWEPT_EDGE",EDGE,{"disambiguationData":[OSD([sQuery(id+"F8.wireOp",EDGE,"E33.top"),sQuery(id+"F8.wireOp",EDGE,"E33.left")])]});
            var Q19;
            Q19=makeQuery(id+"F11.opExtrude","SWEPT_EDGE",EDGE,{"disambiguationData":[OSD([sQuery(id+"F10.wireOp",EDGE,"E46.top"),sQuery(id+"F10.wireOp",EDGE,"E46.left")])]});
            var Q20;
            Q20=makeQuery(id+"F13.opExtrude","SWEPT_EDGE",EDGE,{"disambiguationData":[OSD([sQuery(id+"F12.wireOp",EDGE,"E56.top"),sQuery(id+"F12.wireOp",EDGE,"E56.left")])]});
            var Q21;
            Q21=makeQuery(id+"F15.opExtrude","SWEPT_EDGE",EDGE,{"disambiguationData":[OSD([sQuery(id+"F14.wireOp",EDGE,"E66.bottom"),sQuery(id+"F14.wireOp",EDGE,"E66.left")])]});
            var Q22;
            Q22=makeQuery(id+"F5.opExtrude","SWEPT_EDGE",EDGE,{"disambiguationData":[OSD([sQuery(id+"F4.wireOp",EDGE,"E19.top"),sQuery(id+"F4.wireOp",EDGE,"E19.left")])]});
            var Q23;
            Q23=makeQuery(id+"F9.opExtrude","SWEPT_EDGE",EDGE,{"disambiguationData":[OSD([sQuery(id+"F8.wireOp",EDGE,"E33.bottom"),sQuery(id+"F8.wireOp",EDGE,"E33.left")])]});
            var Q24;
            Q24=makeQuery(id+"F11.opExtrude","SWEPT_EDGE",EDGE,{"disambiguationData":[OSD([sQuery(id+"F10.wireOp",EDGE,"E46.bottom"),sQuery(id+"F10.wireOp",EDGE,"E46.left")])]});
            var Q25;
            Q25=makeQuery(id+"F13.opExtrude","SWEPT_EDGE",EDGE,{"disambiguationData":[OSD([sQuery(id+"F12.wireOp",EDGE,"E56.bottom"),sQuery(id+"F12.wireOp",EDGE,"E56.left")])]});
            var Q26;
            Q26=makeQuery(id+"F15.opExtrude","SWEPT_EDGE",EDGE,{"disambiguationData":[OSD([sQuery(id+"F14.wireOp",EDGE,"E66.top"),sQuery(id+"F14.wireOp",EDGE,"E66.left")])]});
            var Q27;
            Q27=makeQuery(id+"F5.opExtrude","SWEPT_EDGE",EDGE,{"disambiguationData":[OSD([sQuery(id+"F4.wireOp",EDGE,"E19.top"),sQuery(id+"F4.wireOp",EDGE,"E19.right")])]});
            var Q28;
            Q28=makeQuery(id+"F9.opExtrude","SWEPT_EDGE",EDGE,{"disambiguationData":[OSD([sQuery(id+"F8.wireOp",EDGE,"E33.bottom"),sQuery(id+"F8.wireOp",EDGE,"E33.right")])]});
            var Q29;
            Q29=makeQuery(id+"F11.opExtrude","SWEPT_EDGE",EDGE,{"disambiguationData":[OSD([sQuery(id+"F10.wireOp",EDGE,"E46.bottom"),sQuery(id+"F10.wireOp",EDGE,"E46.right")])]});
            var Q30;
            Q30=makeQuery(id+"F13.opExtrude","SWEPT_EDGE",EDGE,{"disambiguationData":[OSD([sQuery(id+"F12.wireOp",EDGE,"E56.bottom"),sQuery(id+"F12.wireOp",EDGE,"E56.right")])]});
            var Q31;
            Q31=makeQuery(id+"F15.opExtrude","SWEPT_EDGE",EDGE,{"disambiguationData":[OSD([sQuery(id+"F14.wireOp",EDGE,"E66.top"),sQuery(id+"F14.wireOp",EDGE,"E66.right")])]});
            var Q32;
            Q32=makeQuery(id+"F15.opExtrude","SWEPT_EDGE",EDGE,{"disambiguationData":[OSD([sQuery(id+"F14.wireOp",EDGE,"E66.bottom"),sQuery(id+"F14.wireOp",EDGE,"E66.right")])]});
            var Q33;
            Q33=makeQuery(id+"F13.opExtrude","SWEPT_EDGE",EDGE,{"disambiguationData":[OSD([sQuery(id+"F12.wireOp",EDGE,"E56.top"),sQuery(id+"F12.wireOp",EDGE,"E56.right")])]});
            var Q34;
            Q34=makeQuery(id+"F11.opExtrude","SWEPT_EDGE",EDGE,{"disambiguationData":[OSD([sQuery(id+"F10.wireOp",EDGE,"E46.top"),sQuery(id+"F10.wireOp",EDGE,"E46.right")])]});
            var Q35;
            Q35=makeQuery(id+"F9.opExtrude","SWEPT_EDGE",EDGE,{"disambiguationData":[OSD([sQuery(id+"F8.wireOp",EDGE,"E33.top"),sQuery(id+"F8.wireOp",EDGE,"E33.right")])]});
            var Q36;
            Q36=makeQuery(id+"F5.opExtrude","SWEPT_EDGE",EDGE,{"disambiguationData":[OSD([sQuery(id+"F4.wireOp",EDGE,"E19.bottom"),sQuery(id+"F4.wireOp",EDGE,"E19.right")])]});
            var Q37;
            Q37=makeQuery(id+"F15.opExtrude","SWEPT_EDGE",EDGE,{"disambiguationData":[OSD([sQuery(id+"F14.wireOp",EDGE,"E67.MirrorCS"),sQuery(id+"F14.wireOp",EDGE,"E68.MirrorCS")])]});
            var Q38;
            Q38=makeQuery(id+"F13.opExtrude","SWEPT_EDGE",EDGE,{"disambiguationData":[OSD([sQuery(id+"F12.wireOp",EDGE,"E57.MirrorCS"),sQuery(id+"F12.wireOp",EDGE,"E59.MirrorCS")])]});
            var Q39;
            Q39=makeQuery(id+"F11.opExtrude","SWEPT_EDGE",EDGE,{"disambiguationData":[OSD([sQuery(id+"F10.wireOp",EDGE,"E47.MirrorCS"),sQuery(id+"F10.wireOp",EDGE,"E48.MirrorCS")])]});
            var Q40;
            Q40=makeQuery(id+"F9.opExtrude","SWEPT_EDGE",EDGE,{"disambiguationData":[OSD([sQuery(id+"F8.wireOp",EDGE,"E35.MirrorCS"),sQuery(id+"F8.wireOp",EDGE,"E36.MirrorCS")])]});
            var Q41;
            Q41=makeQuery(id+"F5.opExtrude","SWEPT_EDGE",EDGE,{"disambiguationData":[OSD([sQuery(id+"F4.wireOp",EDGE,"E20.MirrorCS"),sQuery(id+"F4.wireOp",EDGE,"E22.MirrorCS")])]});
            var Q42;
            Q42=makeQuery(id+"F15.opExtrude","SWEPT_EDGE",EDGE,{"disambiguationData":[OSD([sQuery(id+"F14.wireOp",EDGE,"E67.MirrorCS"),sQuery(id+"F14.wireOp",EDGE,"E69.MirrorCS")])]});
            var Q43;
            Q43=makeQuery(id+"F13.opExtrude","SWEPT_EDGE",EDGE,{"disambiguationData":[OSD([sQuery(id+"F12.wireOp",EDGE,"E58.MirrorCS"),sQuery(id+"F12.wireOp",EDGE,"E59.MirrorCS")])]});
            var Q44;
            Q44=makeQuery(id+"F11.opExtrude","SWEPT_EDGE",EDGE,{"disambiguationData":[OSD([sQuery(id+"F10.wireOp",EDGE,"E47.MirrorCS"),sQuery(id+"F10.wireOp",EDGE,"E49.MirrorCS")])]});
            var Q45;
            Q45=makeQuery(id+"F9.opExtrude","SWEPT_EDGE",EDGE,{"disambiguationData":[OSD([sQuery(id+"F8.wireOp",EDGE,"E34.MirrorCS"),sQuery(id+"F8.wireOp",EDGE,"E35.MirrorCS")])]});
            var Q46;
            Q46=makeQuery(id+"F5.opExtrude","SWEPT_EDGE",EDGE,{"disambiguationData":[OSD([sQuery(id+"F4.wireOp",EDGE,"E22.MirrorCS"),sQuery(id+"F4.wireOp",EDGE,"E23.MirrorCS")])]});
            var Q47;
            Q47=makeQuery(id+"F5.opExtrude","SWEPT_EDGE",EDGE,{"disambiguationData":[OSD([sQuery(id+"F4.wireOp",EDGE,"E21.MirrorCS"),sQuery(id+"F4.wireOp",EDGE,"E23.MirrorCS")])]});
            var Q48;
            Q48=makeQuery(id+"F9.opExtrude","SWEPT_EDGE",EDGE,{"disambiguationData":[OSD([sQuery(id+"F8.wireOp",EDGE,"E34.MirrorCS"),sQuery(id+"F8.wireOp",EDGE,"E37.MirrorCS")])]});
            var Q49;
            Q49=makeQuery(id+"F11.opExtrude","SWEPT_EDGE",EDGE,{"disambiguationData":[OSD([sQuery(id+"F10.wireOp",EDGE,"E49.MirrorCS"),sQuery(id+"F10.wireOp",EDGE,"E50.MirrorCS")])]});
            var Q50;
            Q50=makeQuery(id+"F13.opExtrude","SWEPT_EDGE",EDGE,{"disambiguationData":[OSD([sQuery(id+"F12.wireOp",EDGE,"E58.MirrorCS"),sQuery(id+"F12.wireOp",EDGE,"E60.MirrorCS")])]});
            var Q51;
            Q51=makeQuery(id+"F15.opExtrude","SWEPT_EDGE",EDGE,{"disambiguationData":[OSD([sQuery(id+"F14.wireOp",EDGE,"E69.MirrorCS"),sQuery(id+"F14.wireOp",EDGE,"E70.MirrorCS")])]});
            var Q52;
            Q52=makeQuery(id+"F5.opExtrude","SWEPT_EDGE",EDGE,{"disambiguationData":[OSD([sQuery(id+"F4.wireOp",EDGE,"E20.MirrorCS"),sQuery(id+"F4.wireOp",EDGE,"E21.MirrorCS")])]});
            var Q53;
            Q53=makeQuery(id+"F9.opExtrude","SWEPT_EDGE",EDGE,{"disambiguationData":[OSD([sQuery(id+"F8.wireOp",EDGE,"E36.MirrorCS"),sQuery(id+"F8.wireOp",EDGE,"E37.MirrorCS")])]});
            var Q54;
            Q54=makeQuery(id+"F11.opExtrude","SWEPT_EDGE",EDGE,{"disambiguationData":[OSD([sQuery(id+"F10.wireOp",EDGE,"E48.MirrorCS"),sQuery(id+"F10.wireOp",EDGE,"E50.MirrorCS")])]});
            var Q55;
            Q55=makeQuery(id+"F13.opExtrude","SWEPT_EDGE",EDGE,{"disambiguationData":[OSD([sQuery(id+"F12.wireOp",EDGE,"E57.MirrorCS"),sQuery(id+"F12.wireOp",EDGE,"E60.MirrorCS")])]});
            var Q56;
            Q56=makeQuery(id+"F15.opExtrude","SWEPT_EDGE",EDGE,{"disambiguationData":[OSD([sQuery(id+"F14.wireOp",EDGE,"E68.MirrorCS"),sQuery(id+"F14.wireOp",EDGE,"E70.MirrorCS")])]});
            fillet(context, id + "F16", {"entities" : qUnion([Q0, Q1, Q2, Q3, Q4, Q5, Q6, Q7, Q8, Q9, Q10, Q11, Q12, Q13, Q14, Q15, Q16, Q17, Q18, Q19, Q20, Q21, Q22, Q23, Q24, Q25, Q26, Q27, Q28, Q29, Q30, Q31, Q32, Q33, Q34, Q35, Q36, Q37, Q38, Q39, Q40, Q41, Q42, Q43, Q44, Q45, Q46, Q47, Q48, Q49, Q50, Q51, Q52, Q53, Q54, Q55, Q56]), "radius" : 5 * mm, "tangentPropagation" : true, "allowEdgeOverflow" : false});
        }
        {
            var Q0;
            Q0=makeQuery(id+"F9.opExtrude","SWEPT_EDGE",EDGE,{"disambiguationData":[OSD([sQuery(id+"F8.wireOp",EDGE,"E30.MirrorCS"),sQuery(id+"F8.wireOp",EDGE,"E31.MirrorCS")])]});
            var Q1;
            Q1=makeQuery(id+"F11.opExtrude","SWEPT_EDGE",EDGE,{"disambiguationData":[OSD([sQuery(id+"F10.wireOp",EDGE,"E41.MirrorCS"),sQuery(id+"F10.wireOp",EDGE,"E45.MirrorCS")])]});
            var Q2;
            Q2=makeQuery(id+"F13.opExtrude","SWEPT_EDGE",EDGE,{"disambiguationData":[OSD([sQuery(id+"F12.wireOp",EDGE,"E52.MirrorCS"),sQuery(id+"F12.wireOp",EDGE,"E53.MirrorCS")])]});
            var Q3;
            Q3=makeQuery(id+"F15.opExtrude","SWEPT_EDGE",EDGE,{"disambiguationData":[OSD([sQuery(id+"F14.wireOp",EDGE,"E62.MirrorCS"),sQuery(id+"F14.wireOp",EDGE,"E65.MirrorCS")])]});
            var Q4;
            Q4=makeQuery(id+"F6.opExtrude","SWEPT_EDGE",EDGE,{"disambiguationData":[OSD([sQuery(id+"F4.wireOp",EDGE,"E12.MirrorCS"),sQuery(id+"F4.wireOp",EDGE,"E15.MirrorCS")])]});
            var Q5;
            Q5=makeQuery(id+"F6.opExtrude","SWEPT_EDGE",EDGE,{"disambiguationData":[OSD([sQuery(id+"F4.wireOp",EDGE,"E14.MirrorCS"),sQuery(id+"F4.wireOp",EDGE,"E15.MirrorCS")])]});
            var Q6;
            Q6=makeQuery(id+"F9.opExtrude","SWEPT_EDGE",EDGE,{"disambiguationData":[OSD([sQuery(id+"F8.wireOp",EDGE,"E30.MirrorCS"),sQuery(id+"F8.wireOp",EDGE,"E32.MirrorCS")])]});
            var Q7;
            Q7=makeQuery(id+"F11.opExtrude","SWEPT_EDGE",EDGE,{"disambiguationData":[OSD([sQuery(id+"F10.wireOp",EDGE,"E42.MirrorCS"),sQuery(id+"F10.wireOp",EDGE,"E45.MirrorCS")])]});
            var Q8;
            Q8=makeQuery(id+"F13.opExtrude","SWEPT_EDGE",EDGE,{"disambiguationData":[OSD([sQuery(id+"F12.wireOp",EDGE,"E52.MirrorCS"),sQuery(id+"F12.wireOp",EDGE,"E54.MirrorCS")])]});
            var Q9;
            Q9=makeQuery(id+"F15.opExtrude","SWEPT_EDGE",EDGE,{"disambiguationData":[OSD([sQuery(id+"F14.wireOp",EDGE,"E62.MirrorCS"),sQuery(id+"F14.wireOp",EDGE,"E64.MirrorCS")])]});
            var Q10;
            Q10=makeQuery(id+"F15.opExtrude","SWEPT_EDGE",EDGE,{"disambiguationData":[OSD([sQuery(id+"F14.wireOp",EDGE,"E63.MirrorCS"),sQuery(id+"F14.wireOp",EDGE,"E64.MirrorCS")])]});
            var Q11;
            Q11=makeQuery(id+"F13.opExtrude","SWEPT_EDGE",EDGE,{"disambiguationData":[OSD([sQuery(id+"F12.wireOp",EDGE,"E54.MirrorCS"),sQuery(id+"F12.wireOp",EDGE,"E55.MirrorCS")])]});
            var Q12;
            Q12=makeQuery(id+"F9.opExtrude","SWEPT_EDGE",EDGE,{"disambiguationData":[OSD([sQuery(id+"F8.wireOp",EDGE,"E28.MirrorCS"),sQuery(id+"F8.wireOp",EDGE,"E32.MirrorCS")])]});
            var Q13;
            Q13=makeQuery(id+"F6.opExtrude","SWEPT_EDGE",EDGE,{"disambiguationData":[OSD([sQuery(id+"F4.wireOp",EDGE,"E14.MirrorCS"),sQuery(id+"F4.wireOp",EDGE,"E16.MirrorCS")])]});
            var Q14;
            Q14=makeQuery(id+"F11.opExtrude","SWEPT_EDGE",EDGE,{"disambiguationData":[OSD([sQuery(id+"F10.wireOp",EDGE,"E42.MirrorCS"),sQuery(id+"F10.wireOp",EDGE,"E44.MirrorCS")])]});
            var Q15;
            Q15=makeQuery(id+"F6.opExtrude","SWEPT_EDGE",EDGE,{"disambiguationData":[OSD([sQuery(id+"F4.wireOp",EDGE,"E12.MirrorCS"),sQuery(id+"F4.wireOp",EDGE,"E16.MirrorCS")])]});
            var Q16;
            Q16=makeQuery(id+"F9.opExtrude","SWEPT_EDGE",EDGE,{"disambiguationData":[OSD([sQuery(id+"F8.wireOp",EDGE,"E28.MirrorCS"),sQuery(id+"F8.wireOp",EDGE,"E31.MirrorCS")])]});
            var Q17;
            Q17=makeQuery(id+"F11.opExtrude","SWEPT_EDGE",EDGE,{"disambiguationData":[OSD([sQuery(id+"F10.wireOp",EDGE,"E41.MirrorCS"),sQuery(id+"F10.wireOp",EDGE,"E44.MirrorCS")])]});
            var Q18;
            Q18=makeQuery(id+"F13.opExtrude","SWEPT_EDGE",EDGE,{"disambiguationData":[OSD([sQuery(id+"F12.wireOp",EDGE,"E53.MirrorCS"),sQuery(id+"F12.wireOp",EDGE,"E55.MirrorCS")])]});
            var Q19;
            Q19=makeQuery(id+"F15.opExtrude","SWEPT_EDGE",EDGE,{"disambiguationData":[OSD([sQuery(id+"F14.wireOp",EDGE,"E63.MirrorCS"),sQuery(id+"F14.wireOp",EDGE,"E65.MirrorCS")])]});
            fillet(context, id + "F17", {"entities" : qUnion([Q0, Q1, Q2, Q3, Q4, Q5, Q6, Q7, Q8, Q9, Q10, Q11, Q12, Q13, Q14, Q15, Q16, Q17, Q18, Q19]), "radius" : 5 * mm, "tangentPropagation" : true, "allowEdgeOverflow" : false});
        }
        {
            var Q0;
            Q0=makeQuery(id+"F15.opExtrude","CAP_FACE",FACE,{"disambiguationData":[OSD([sQuery(id+"F14.wireOp",EDGE,"E61.bottom"),sQuery(id+"F14.wireOp",EDGE,"E61.top"),sQuery(id+"F14.wireOp",EDGE,"E61.left"),sQuery(id+"F14.wireOp",EDGE,"E61.right")])],"isStart":false});
            var sketch = newSketch(context, id + "F18", { "sketchPlane" : qUnion([Q0])});
            skLineSegment(sketch, "E71.bottom", {"start": v(-565, 232) * mm, "end": v(-435.04, 232) * mm});
            skLineSegment(sketch, "E71.top", {"start": v(-565, 114) * mm, "end": v(-435.04, 114) * mm});
            skLineSegment(sketch, "E71.left", {"start": v(-565, 232) * mm, "end": v(-565, 114) * mm});
            skLineSegment(sketch, "E71.right", {"start": v(-435.04, 232) * mm, "end": v(-435.04, 114) * mm});
            skLineSegment(sketch, "E72.MirrorCS", {"start": v(565, 114) * mm, "end": v(435.04, 114) * mm});
            skLineSegment(sketch, "E73.MirrorCS", {"start": v(565, 232) * mm, "end": v(435.04, 232) * mm});
            skLineSegment(sketch, "E74.MirrorCS", {"start": v(435.04, 232) * mm, "end": v(435.04, 114) * mm});
            skLineSegment(sketch, "E75.MirrorCS", {"start": v(565, 232) * mm, "end": v(565, 114) * mm});
            skLineSegment(sketch, "E76.bottom", {"start": v(-571.05, -117.91) * mm, "end": v(-441, -117.91) * mm});
            skLineSegment(sketch, "E76.top", {"start": v(-571.05, -196) * mm, "end": v(-441, -196) * mm});
            skLineSegment(sketch, "E76.left", {"start": v(-571.05, -117.91) * mm, "end": v(-571.05, -196) * mm});
            skLineSegment(sketch, "E76.right", {"start": v(-441, -117.91) * mm, "end": v(-441, -196) * mm});
            skLineSegment(sketch, "E77.MirrorCS", {"start": v(571.05, -117.91) * mm, "end": v(441, -117.91) * mm});
            skLineSegment(sketch, "E78.MirrorCS", {"start": v(441, -117.91) * mm, "end": v(441, -196) * mm});
            skLineSegment(sketch, "E79.MirrorCS", {"start": v(571.05, -196) * mm, "end": v(441, -196) * mm});
            skLineSegment(sketch, "E80.MirrorCS", {"start": v(571.05, -117.91) * mm, "end": v(571.05, -196) * mm});
            skSolve(sketch);
        }
        {
            var Q0;
            Q0 = qSketchRegion(id + "F18", true);
            extrude(context, id + "F19", {"entities" : qUnion([Q0]), "depth" : 6 * mm, "offsetDistance" : 25 * mm});
        }
        {
            var Q0;
            Q0=makeQuery(id+"F19.opExtrude","SWEPT_EDGE",EDGE,{"disambiguationData":[OSD([sQuery(id+"F18.wireOp",EDGE,"E71.bottom"),sQuery(id+"F18.wireOp",EDGE,"E71.right")])]});
            var Q1;
            Q1=makeQuery(id+"F19.opExtrude","SWEPT_EDGE",EDGE,{"disambiguationData":[OSD([sQuery(id+"F18.wireOp",EDGE,"E71.bottom"),sQuery(id+"F18.wireOp",EDGE,"E71.left")])]});
            var Q2;
            Q2=makeQuery(id+"F19.opExtrude","SWEPT_EDGE",EDGE,{"disambiguationData":[OSD([sQuery(id+"F18.wireOp",EDGE,"E71.top"),sQuery(id+"F18.wireOp",EDGE,"E71.left")])]});
            var Q3;
            Q3=makeQuery(id+"F19.opExtrude","SWEPT_EDGE",EDGE,{"disambiguationData":[OSD([sQuery(id+"F18.wireOp",EDGE,"E71.top"),sQuery(id+"F18.wireOp",EDGE,"E71.right")])]});
            var Q4;
            Q4=makeQuery(id+"F19.opExtrude","SWEPT_EDGE",EDGE,{"disambiguationData":[OSD([sQuery(id+"F18.wireOp",EDGE,"E72.MirrorCS"),sQuery(id+"F18.wireOp",EDGE,"E75.MirrorCS")])]});
            var Q5;
            Q5=makeQuery(id+"F19.opExtrude","SWEPT_EDGE",EDGE,{"disambiguationData":[OSD([sQuery(id+"F18.wireOp",EDGE,"E72.MirrorCS"),sQuery(id+"F18.wireOp",EDGE,"E74.MirrorCS")])]});
            var Q6;
            Q6=makeQuery(id+"F19.opExtrude","SWEPT_EDGE",EDGE,{"disambiguationData":[OSD([sQuery(id+"F18.wireOp",EDGE,"E73.MirrorCS"),sQuery(id+"F18.wireOp",EDGE,"E74.MirrorCS")])]});
            var Q7;
            Q7=makeQuery(id+"F19.opExtrude","SWEPT_EDGE",EDGE,{"disambiguationData":[OSD([sQuery(id+"F18.wireOp",EDGE,"E73.MirrorCS"),sQuery(id+"F18.wireOp",EDGE,"E75.MirrorCS")])]});
            fillet(context, id + "F20", {"entities" : qUnion([Q0, Q1, Q2, Q3, Q4, Q5, Q6, Q7]), "radius" : 5 * mm, "tangentPropagation" : true, "allowEdgeOverflow" : false});
        }
        {
            var Q0;
            Q0=makeQuery(id+"F19.opExtrude","SWEPT_EDGE",EDGE,{"disambiguationData":[OSD([sQuery(id+"F18.wireOp",EDGE,"E76.bottom"),sQuery(id+"F18.wireOp",EDGE,"E76.right")])]});
            var Q1;
            Q1=makeQuery(id+"F19.opExtrude","SWEPT_EDGE",EDGE,{"disambiguationData":[OSD([sQuery(id+"F18.wireOp",EDGE,"E76.top"),sQuery(id+"F18.wireOp",EDGE,"E76.right")])]});
            var Q2;
            Q2=makeQuery(id+"F19.opExtrude","SWEPT_EDGE",EDGE,{"disambiguationData":[OSD([sQuery(id+"F18.wireOp",EDGE,"E76.bottom"),sQuery(id+"F18.wireOp",EDGE,"E76.left")])]});
            var Q3;
            Q3=makeQuery(id+"F19.opExtrude","SWEPT_EDGE",EDGE,{"disambiguationData":[OSD([sQuery(id+"F18.wireOp",EDGE,"E76.top"),sQuery(id+"F18.wireOp",EDGE,"E76.left")])]});
            var Q4;
            Q4=makeQuery(id+"F19.opExtrude","SWEPT_EDGE",EDGE,{"disambiguationData":[OSD([sQuery(id+"F18.wireOp",EDGE,"E77.MirrorCS"),sQuery(id+"F18.wireOp",EDGE,"E78.MirrorCS")])]});
            var Q5;
            Q5=makeQuery(id+"F19.opExtrude","SWEPT_EDGE",EDGE,{"disambiguationData":[OSD([sQuery(id+"F18.wireOp",EDGE,"E78.MirrorCS"),sQuery(id+"F18.wireOp",EDGE,"E79.MirrorCS")])]});
            var Q6;
            Q6=makeQuery(id+"F19.opExtrude","SWEPT_EDGE",EDGE,{"disambiguationData":[OSD([sQuery(id+"F18.wireOp",EDGE,"E79.MirrorCS"),sQuery(id+"F18.wireOp",EDGE,"E80.MirrorCS")])]});
            var Q7;
            Q7=makeQuery(id+"F19.opExtrude","SWEPT_EDGE",EDGE,{"disambiguationData":[OSD([sQuery(id+"F18.wireOp",EDGE,"E77.MirrorCS"),sQuery(id+"F18.wireOp",EDGE,"E80.MirrorCS")])]});
            fillet(context, id + "F21", {"entities" : qUnion([Q0, Q1, Q2, Q3, Q4, Q5, Q6, Q7]), "radius" : 5 * mm, "tangentPropagation" : true, "allowEdgeOverflow" : false});
        }
        {
            var Q0;
            Q0=makeQuery(id+"F19.opExtrude","CAP_FACE",FACE,{"disambiguationData":[OSD([sQuery(id+"F18.wireOp",EDGE,"E71.bottom"),sQuery(id+"F18.wireOp",EDGE,"E71.top"),sQuery(id+"F18.wireOp",EDGE,"E71.left"),sQuery(id+"F18.wireOp",EDGE,"E71.right")])],"isStart":false});
            var sketch = newSketch(context, id + "F22", { "sketchPlane" : qUnion([Q0])});
            skCircle(sketch, "E81", {"center": v(-500, 144) * mm, "radius": 3.75 * mm});
            skCircle(sketch, "E82.MirrorC", {"center": v(500, 144) * mm, "radius": 3.75 * mm});
            skCircle(sketch, "E83", {"center": v(-500, -164) * mm, "radius": 3.75 * mm});
            skCircle(sketch, "E84.MirrorC", {"center": v(500, -164) * mm, "radius": 3.75 * mm});
            skSolve(sketch);
        }
        {
            var Q0;
            Q0 = qSketchRegion(id + "F22", true);
            extrude(context, id + "F23", {"entities" : qUnion([Q0]), "operationType" : NewBodyOperationType.REMOVE, "oppositeDirection" : true, "depth" : 50 * mm, "offsetDistance" : 25 * mm});
        }
        {
            var Q0;
            Q0=makeQuery(id+"F1.opExtrude","CAP_FACE",FACE,{"disambiguationData":[OSD([sQuery(id+"F0.wireOp",EDGE,"E0.bottom"),sQuery(id+"F0.wireOp",EDGE,"E0.top"),sQuery(id+"F0.wireOp",EDGE,"E0.left"),sQuery(id+"F0.wireOp",EDGE,"E0.right")])],"isStart":false});
            var sketch = newSketch(context, id + "F24", { "sketchPlane" : qUnion([Q0])});
            skLineSegment(sketch, "E85.bottom", {"start": v(-306.2, -196) * mm, "end": v(-196.2, -196) * mm});
            skLineSegment(sketch, "E85.top", {"start": v(-306.2, -116) * mm, "end": v(-196.2, -116) * mm});
            skLineSegment(sketch, "E85.left", {"start": v(-306.2, -196) * mm, "end": v(-306.2, -116) * mm});
            skLineSegment(sketch, "E85.right", {"start": v(-196.2, -196) * mm, "end": v(-196.2, -116) * mm});
            skLineSegment(sketch, "E86", {"start": v(-631.74, -196) * mm, "end": v(-148.82, -196) * mm, "construction": true});
            skSolve(sketch);
        }
        {
            var Q0;
            Q0 = qSketchRegion(id + "F24", true);
            extrude(context, id + "F25", {"entities" : qUnion([Q0]), "depth" : 40 * mm, "offsetDistance" : 25 * mm});
        }
        {
            var Q0;
            Q0=makeQuery(id+"F6.opExtrude","SWEPT_EDGE",EDGE,{"disambiguationData":[OSD([sQuery(id+"F4.wireOp",EDGE,"E19.top"),sQuery(id+"F4.wireOp",EDGE,"E19.right")])]});
            fillet(context, id + "F26", {"entities" : qUnion([Q0]), "radius" : 5 * mm, "tangentPropagation" : true, "allowEdgeOverflow" : false});
        }
        {
            var Q0;
            Q0=makeQuery(id+"F1.opExtrude","CAP_FACE",FACE,{"disambiguationData":[OSD([sQuery(id+"F0.wireOp",EDGE,"E0.bottom"),sQuery(id+"F0.wireOp",EDGE,"E0.top"),sQuery(id+"F0.wireOp",EDGE,"E0.left"),sQuery(id+"F0.wireOp",EDGE,"E0.right")])],"isStart":false});
            var sketch = newSketch(context, id + "F27", { "sketchPlane" : qUnion([Q0])});
            skLineSegment(sketch, "E87.bottom", {"start": v(-435.04, 218) * mm, "end": v(435.04, 218) * mm});
            skLineSegment(sketch, "E87.top", {"start": v(-435.04, 198) * mm, "end": v(435.04, 198) * mm});
            skLineSegment(sketch, "E87.left", {"start": v(-435.04, 218) * mm, "end": v(-435.04, 198) * mm});
            skLineSegment(sketch, "E87.right", {"start": v(435.04, 218) * mm, "end": v(435.04, 198) * mm});
            skPoint(sketch, "E87.middle", {"position": v(0, 208) * mm});
            skSolve(sketch);
        }
        {
            var Q0;
            Q0 = qSketchRegion(id + "F27", true);
            extrude(context, id + "F28", {"entities" : qUnion([Q0]), "depth" : 18 * mm, "offsetDistance" : 25 * mm});
        }
        {
            var Q0;
            Q0 = qConstructionFilter(qBodyType(qCreatedBy(id + "F27" ,EDGE), BodyType.WIRE), ConstructionObject.NO);
            extrude(context, id + "F29", {"bodyType" : ToolBodyType.SURFACE, "surfaceEntities" : qUnion([Q0]), "depth" : 18 * mm, "offsetDistance" : 25 * mm});
        }
        {
            var Q0;
            Q0=makeQuery(id+"F1.opExtrude","SWEPT_EDGE",EDGE,{"disambiguationData":[OSD([sQuery(id+"F0.wireOp",EDGE,"E0.bottom"),sQuery(id+"F0.wireOp",EDGE,"E0.left")])]});
            var Q1;
            Q1=makeQuery(id+"F1.opExtrude","SWEPT_EDGE",EDGE,{"disambiguationData":[OSD([sQuery(id+"F0.wireOp",EDGE,"E0.top"),sQuery(id+"F0.wireOp",EDGE,"E0.left")])]});
            var Q2;
            Q2=makeQuery(id+"F1.opExtrude","SWEPT_EDGE",EDGE,{"disambiguationData":[OSD([sQuery(id+"F0.wireOp",EDGE,"E0.bottom"),sQuery(id+"F0.wireOp",EDGE,"E0.right")])]});
            var Q3;
            Q3=makeQuery(id+"F1.opExtrude","SWEPT_EDGE",EDGE,{"disambiguationData":[OSD([sQuery(id+"F0.wireOp",EDGE,"E0.top"),sQuery(id+"F0.wireOp",EDGE,"E0.right")])]});
            fillet(context, id + "F30", {"entities" : qUnion([Q0, Q1, Q2, Q3]), "radius" : 5 * mm, "tangentPropagation" : true, "allowEdgeOverflow" : false});
        }
        {
            var Q0;
            Q0=makeQuery(id+"F19.opExtrude","CAP_FACE",FACE,{"disambiguationData":[OSD([sQuery(id+"F18.wireOp",EDGE,"E71.bottom"),sQuery(id+"F18.wireOp",EDGE,"E71.top"),sQuery(id+"F18.wireOp",EDGE,"E71.left"),sQuery(id+"F18.wireOp",EDGE,"E71.right")])],"isStart":false});
            var sketch = newSketch(context, id + "F31", { "sketchPlane" : qUnion([Q0])});
            skLineSegment(sketch, "E88.bottom", {"start": v(-565, 164) * mm, "end": v(-435.04, 164) * mm});
            skLineSegment(sketch, "E88.top", {"start": v(-565, 114) * mm, "end": v(-435.04, 114) * mm});
            skLineSegment(sketch, "E88.left", {"start": v(-565, 164) * mm, "end": v(-565, 114) * mm});
            skLineSegment(sketch, "E88.right", {"start": v(-435.04, 164) * mm, "end": v(-435.04, 114) * mm});
            skLineSegment(sketch, "E89.MirrorCS", {"start": v(565, 164) * mm, "end": v(435.04, 164) * mm});
            skLineSegment(sketch, "E90.MirrorCS", {"start": v(565, 164) * mm, "end": v(565, 114) * mm});
            skLineSegment(sketch, "E91.MirrorCS", {"start": v(435.04, 164) * mm, "end": v(435.04, 114) * mm});
            skLineSegment(sketch, "E92.MirrorCS", {"start": v(565, 114) * mm, "end": v(435.04, 114) * mm});
            skSolve(sketch);
        }
        {
            var Q0;
            Q0 = qSketchRegion(id + "F31", true);
            extrude(context, id + "F32", {"entities" : qUnion([Q0]), "operationType" : NewBodyOperationType.REMOVE, "oppositeDirection" : true, "depth" : 6 * mm, "offsetDistance" : 25 * mm});
        }
    });
